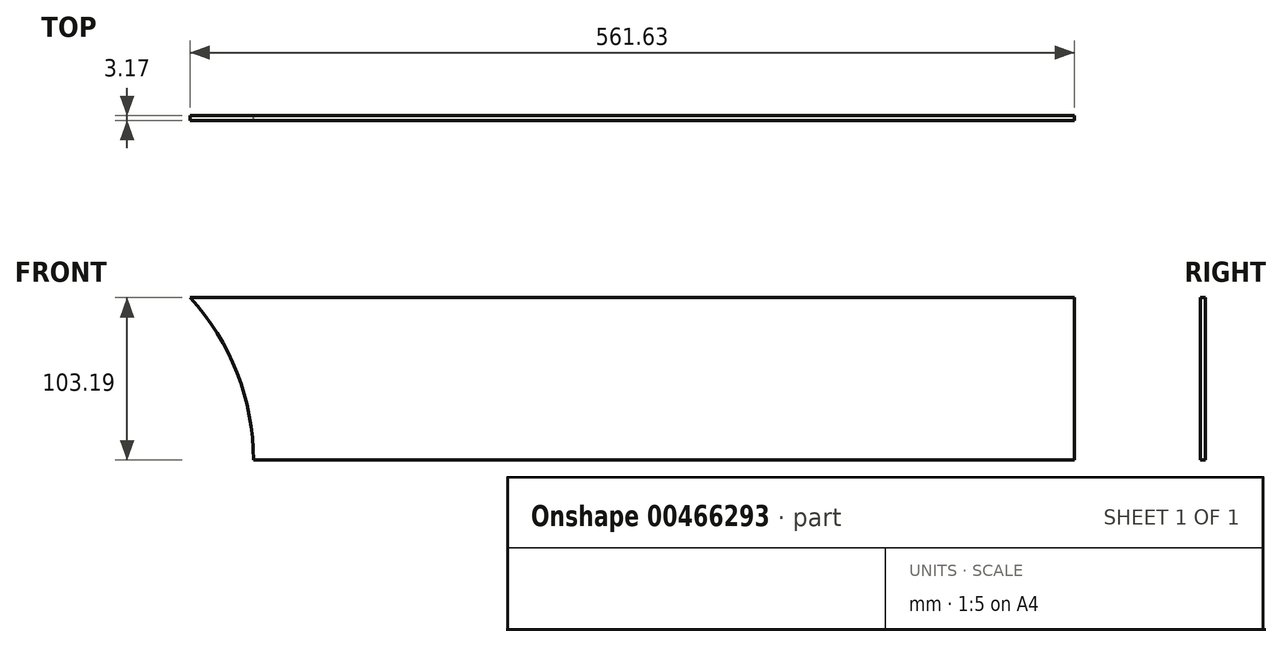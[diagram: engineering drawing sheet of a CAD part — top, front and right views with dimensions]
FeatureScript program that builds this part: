
annotation { "Feature Type Name" : "Feature", "Feature Type Description" : "" }
export const myFeature = defineFeature(function(context is Context, id is Id, definition is map)
    precondition{}
    {
        {
            var Q0;
            Q0=qCreatedBy(makeId("Front.planeOp"),FACE);
            var sketch = newSketch(context, id + "F0", { "sketchPlane" : qUnion([Q0])});
            skLineSegment(sketch, "E0", {"start": v(-358.65, 126.35) * mm, "end": v(202.98, 126.35) * mm});
            skLineSegment(sketch, "E1", {"start": v(202.98, 126.35) * mm, "end": v(202.98, 23.16) * mm});
            skLineSegment(sketch, "E2", {"start": v(202.98, 23.16) * mm, "end": v(-318.4, 23.16) * mm});
            skArc(sketch, "E3", {"start": v(-318.4, 23.16) * mm, "mid": v(-328.82, 78.54) * mm, "end": v(-358.65, 126.35) * mm});
            skSolve(sketch);
        }
        {
            var Q0;
            Q0=qSketchRegion(id+"F0",true);
            extrude(context, id + "F1", {"entities" : qUnion([Q0]), "depth" : 3.17 * mm, "offsetDistance" : 25.4 * mm});
        }
    });
